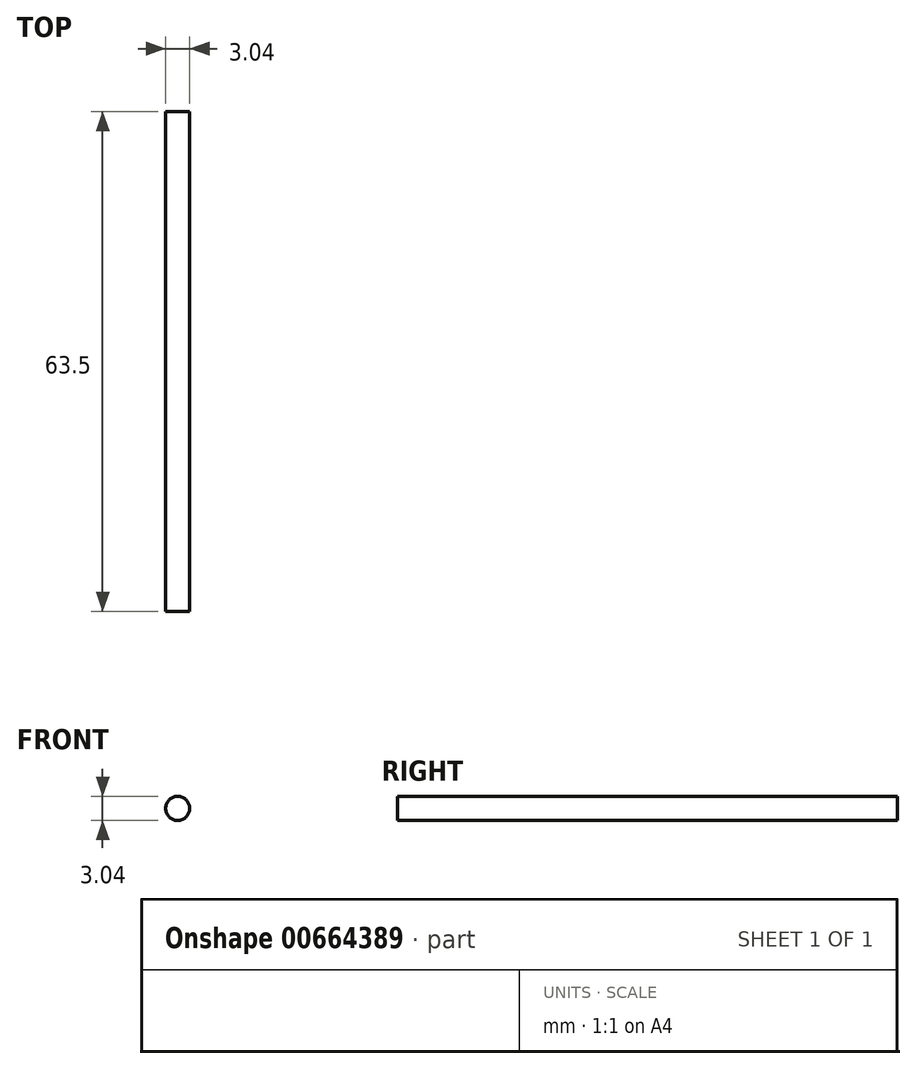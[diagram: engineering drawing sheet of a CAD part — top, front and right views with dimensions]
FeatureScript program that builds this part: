
annotation { "Feature Type Name" : "Feature", "Feature Type Description" : "" }
export const myFeature = defineFeature(function(context is Context, id is Id, definition is map)
    precondition{}
    {
        {
            var Q0;
            Q0=qCreatedBy(makeId("Front.planeOp"),FACE);
            var sketch = newSketch(context, id + "F0", { "sketchPlane" : qUnion([Q0])});
            skCircle(sketch, "E0", {"center": v(0, 0) * mm, "radius": 1.52 * mm});
            skSolve(sketch);
        }
        {
            var Q0;
            Q0 = qSketchRegion(id + "F0", true);
            extrude(context, id + "F1", {"entities" : qUnion([Q0]), "oppositeDirection" : true, "depth" : 63.5 * mm, "offsetDistance" : 25.4 * mm});
        }
    });
